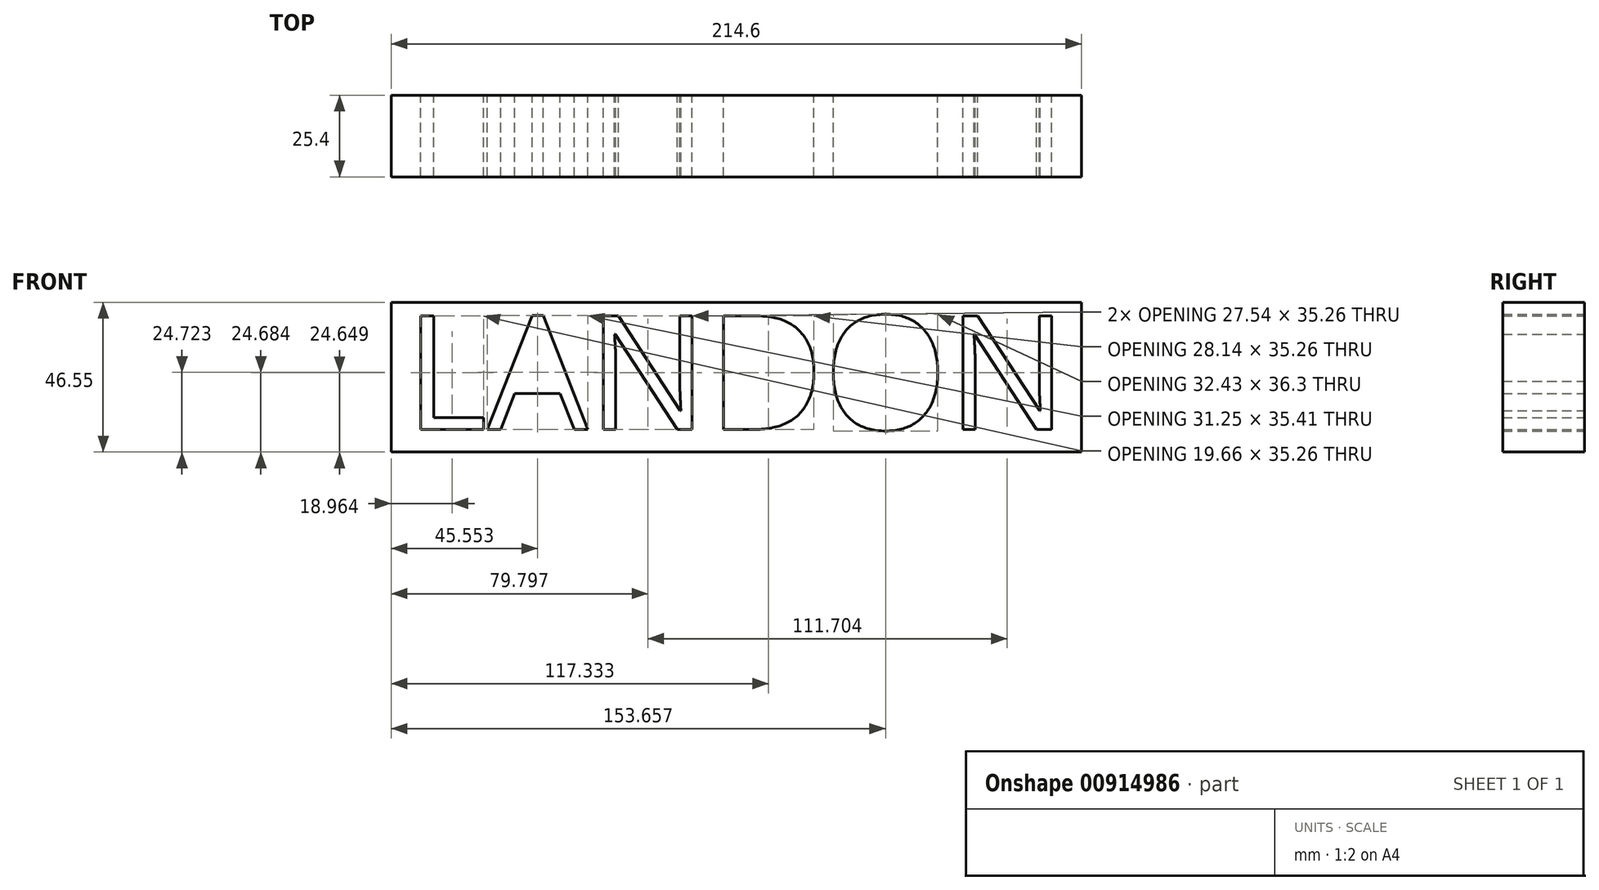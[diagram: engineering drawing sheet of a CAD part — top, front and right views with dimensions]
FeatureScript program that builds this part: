
annotation { "Feature Type Name" : "Feature", "Feature Type Description" : "" }
export const myFeature = defineFeature(function(context is Context, id is Id, definition is map)
    precondition{}
    {
        {
            var Q0;
            Q0=qCreatedBy(makeId("Front.planeOp"),FACE);
            var sketch = newSketch(context, id + "F0", { "sketchPlane" : qUnion([Q0])});
            skText(sketch, "E0", { "text": "LANDON\n", "fontName": "OpenSans-Regular.ttf"});
            skLineSegment(sketch, "E1.bottom", {"start": v(-67.88, 48.9) * mm, "end": v(146.72, 48.9) * mm});
            skLineSegment(sketch, "E1.top", {"start": v(-67.88, 2.35) * mm, "end": v(146.72, 2.35) * mm});
            skLineSegment(sketch, "E1.left", {"start": v(-67.88, 48.9) * mm, "end": v(-67.88, 2.35) * mm});
            skLineSegment(sketch, "E1.right", {"start": v(146.72, 48.9) * mm, "end": v(146.72, 2.35) * mm});
            const initialGuessF0  = {"E0": [-0.06359, 0.00937, 1, 0, 0.03556]};
            skSetInitialGuess(sketch, initialGuessF0);
            skSolve(sketch);
        }
        {
            var Q0;
            Q0 = qSketchRegion(id + "F0", true);
            extrude(context, id + "F1", {"entities" : qUnion([Q0]), "depth" : 25.4 * mm, "offsetDistance" : 25.4 * mm});
        }
    });
